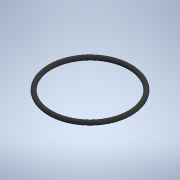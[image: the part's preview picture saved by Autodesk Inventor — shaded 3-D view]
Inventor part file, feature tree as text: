
AUTODESK INVENTOR PART (.ipt)
format: ipt  version: 2020 (Build 240168000, 168)  size: 119,808 bytes
history: native  units: mm
features: revolve x1, sketch x1
ambient origin geometry x8: Origin, YZ Plane, XZ Plane, XY Plane, X Axis, Y Axis, Z Axis, Center Point
bodies: Solid1 (feature_tree)
feature tree (2):
  revolve  "Revolution1"  [1 undecoded]
  sketch  "Sketch1"  dims[d0=1.78mm d1=16.625mm d2=90.0deg]
note: 1 required parameter value undecoded (feature->parameter linkage not recoverable at this tier; creation-order binding heuristic only, values carry confidence <= 0.55)
